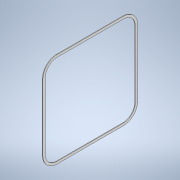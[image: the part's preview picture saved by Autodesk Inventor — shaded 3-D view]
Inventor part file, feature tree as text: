
AUTODESK INVENTOR PART (.ipt)
format: ipt  version: 2020 (Build 240168000, 168)  size: 128,512 bytes
history: native  units: mm
features: extrude x2, sketch x2, other x1, projected_geometry x1
ambient origin geometry x8: Origin, YZ Plane, XZ Plane, XY Plane, X Axis, Y Axis, Z Axis, Center Point
bodies: Body1 (feature_tree)
feature tree (6):
  other  "Твердое тело1"
  extrude  "Выдавливание1"  Depth=200.666mm
  extrude  "Выдавливание2"  Depth=200.666mm
  sketch  "Эскиз1"
  sketch  "Эскиз2"
  projected_geometry  "Спроецированная петля1"
